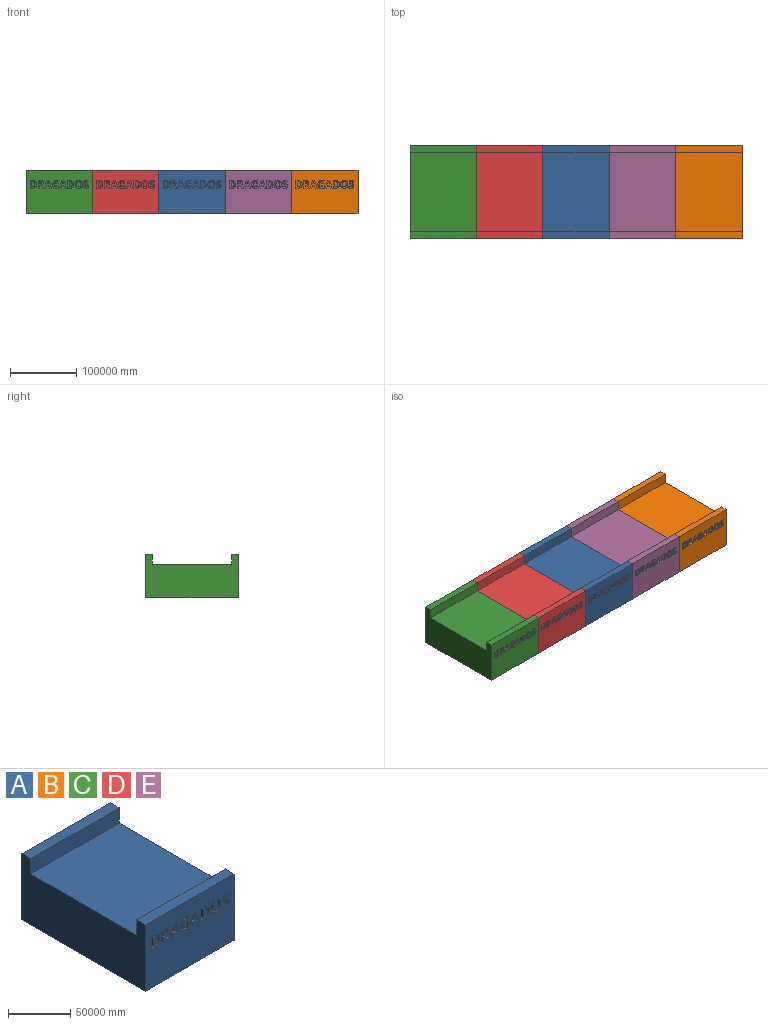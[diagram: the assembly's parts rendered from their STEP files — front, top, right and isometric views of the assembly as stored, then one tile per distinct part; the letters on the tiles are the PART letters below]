
ASSEMBLY  parts=5 mates=4
PART A: 152 faces, bbox 100000x140000x65000 mm
  f0: plane 100000x65000mm, normal (0,-1,0), area 5889989465.6mm2, adj f2,f3,f4,f9,f10,f11,f12,f13
  f1: plane 120000x100000mm, normal (0,0,1), area 12000000000mm2, adj f2,f4,f6,f8
  f2: plane 140000x65000mm, normal (-1,0,0), area 7300000000mm2, adj f0,f1,f3,f5,f6,f7,f8,f9
  f3: plane 140000x100000mm, normal (0,0,-1), area 14000000000mm2, adj f0,f2,f4,f5
  f4: plane 140000x65000mm, normal (1,0,0), area 7300000000mm2, adj f0,f1,f3,f5,f6,f7,f8,f9
  f5: plane 100000x65000mm, normal (0,1,0), area 6500000000mm2, adj f2,f3,f4,f7
  f6: plane 100000x15000mm, normal (0,-1,0), area 1500000000mm2, adj f1,f2,f4,f7
  f7: plane 100000x10000mm, normal (0,0,1), area 1000000000mm2, adj f2,f4,f5,f6
  f8: plane 100000x15000mm, normal (0,1,0), area 1500000000mm2, adj f1,f2,f4,f9
  f9: plane 100000x10000mm, normal (0,0,1), area 1000000000mm2, adj f0,f2,f4,f8
  f10: plane 4511.8x3000mm, normal (0,0,-1), area 13535406.6mm2, adj f0,f11,f28,f29
  f11: plane 3000x2008.29mm, normal (1,0,0), area 6024861.1mm2, adj f0,f10,f12,f29
  f12: plane 3000x2155.11mm, normal (0,0,1), area 6465340.4mm2, adj f0,f11,f13,f29
  f13: plane 3000x2371.62mm, normal (1,0,0), area 7114860.7mm2, adj f0,f12,f14,f29
  f14: extruded ~3000x1532.97mm, area 4629580.4mm2, adj f0,f13,f15,f29
  f15: extruded ~3000x2203.64mm, area 7506016mm2, adj f0,f14,f16,f29
  f16: extruded ~3000x2827.03mm, area 8939362.1mm2, adj f0,f15,f17,f29
  f17: extruded ~3000x2822.05mm, area 9132796.1mm2, adj f0,f16,f18,f29
  f18: extruded ~3000x2503.52mm, area 8406838mm2, adj f0,f17,f19,f29
  f19: extruded ~3000x2590.62mm, area 8066421.4mm2, adj f0,f18,f20,f29
  f20: plane 3000x1928.65mm, normal (-0.92,0,0.38), area 6265491.2mm2, adj f0,f19,f21,f29
  f21: extruded ~3377.01x3000mm, area 10418684.1mm2, adj f0,f20,f22,f29
  f22: extruded ~4364.98x3000mm, area 14252224.5mm2, adj f0,f21,f23,f29
  f23: extruded ~4291.56x3000mm, area 14101973.1mm2, adj f0,f22,f24,f29
  f24: extruded ~4345.07x3000mm, area 13969649.8mm2, adj f0,f23,f25,f29
  f25: extruded ~3930.72x3000mm, area 13034389.8mm2, adj f0,f24,f26,f29
  f26: extruded ~3000x1978.42mm, area 5956492.1mm2, adj f0,f25,f27,f29
  f27: extruded ~3000x2065.52mm, area 6384867.5mm2, adj f0,f26,f28,f29
  f28: plane 5895.45x3000mm, normal (-1,0,0), area 17686364.2mm2, adj f0,f10,f27,f29
  f29: plane 11688.88x9332.19mm, normal (0,-1,0), area 62986172mm2, adj f10,f11,f12,f13,f14,f15,f16,f17
  f30: extruded ~3000x2870.58mm, area 9030077.2mm2, adj f31,f43,f44,f147
  f31: extruded ~3000x2871.83mm, area 9041235.7mm2, adj f30,f32,f44,f147
  f32: extruded ~3000x2168.8mm, area 7406378.6mm2, adj f31,f33,f44,f147
  f33: extruded ~3839.88x3000mm, area 16403148.1mm2, adj f32,f34,f44,f147
  f34: extruded ~3834.91x3000mm, area 16424551mm2, adj f33,f43,f44,f147
  f35: extruded ~4341.33x3000mm, area 14012505mm2, adj f0,f36,f42,f44
  f36: extruded ~4338.85x3000mm, area 13992602.8mm2, adj f0,f35,f37,f44
  f37: extruded ~4009.11x3000mm, area 13243213.6mm2, adj f0,f36,f38,f44
  f38: extruded ~4024.04x3000mm, area 13263273.8mm2, adj f0,f37,f39,f44
  f39: extruded ~4336.36x3000mm, area 14008077.7mm2, adj f0,f38,f40,f44
  f40: extruded ~4356.27x3000mm, area 14055744mm2, adj f0,f39,f41,f44
  f41: extruded ~4012.84x3000mm, area 13261248.6mm2, adj f0,f40,f42,f44
  f42: extruded ~4012.84x3000mm, area 13261248.6mm2, adj f0,f35,f41,f44
  f43: extruded ~3000x2161.34mm, area 7382216.9mm2, adj f30,f34,f44,f147
  f44: plane 11706.3x10825.34mm, normal (0,-1,0), area 67703911.6mm2, adj f30,f31,f32,f33,f34,f35,f36,f37
  f45: extruded ~3663.2x3235.16mm, area 16809076.1mm2, adj f46,f56,f57,f148
  f46: extruded ~3740.34x3484.02mm, area 17594489.8mm2, adj f45,f47,f57,f148
  f47: plane 3000x1032.76mm, normal (0,0,-1), area 3098286.7mm2, adj f46,f48,f57,f148
  f48: plane 7403.54x3000mm, normal (-1,0,0), area 22210609.3mm2, adj f47,f56,f57,f148
  f49: extruded ~4300.27x3000mm, area 14174793.3mm2, adj f0,f50,f55,f57
  f50: extruded ~4107.41x3000mm, area 13544800.3mm2, adj f0,f49,f51,f57
  f51: extruded ~4325.16x3000mm, area 14051984.7mm2, adj f0,f50,f52,f57
  f52: plane 3568.63x3000mm, normal (0,0,-1), area 10705887mm2, adj f0,f51,f53,f57
  f53: plane 11370.34x3000mm, normal (1,0,0), area 34111016.4mm2, adj f0,f52,f54,f57
  f54: plane 3220.23x3000mm, normal (0,0,1), area 9660681.8mm2, adj f0,f53,f55,f57
  f55: extruded ~4615.08x3000mm, area 14906133.2mm2, adj f0,f49,f54,f57
  f56: plane 3000x1281.62mm, normal (0,0,1), area 3844861.8mm2, adj f45,f48,f57,f148
  f57: plane 11370.34x9434.22mm, normal (0,-1,0), area 65817079.6mm2, adj f45,f46,f47,f48,f49,f50,f51,f52
  f58: extruded ~4160.91x3000mm, area 13065876.7mm2, adj f59,f69,f70,f149
  f59: plane 3000x2961.41mm, normal (0,0,-1), area 8884243.7mm2, adj f58,f60,f70,f149
  f60: extruded ~4922.42x3000mm, area 15410954.9mm2, adj f59,f69,f70,f149
  f61: plane 3000x2707.58mm, normal (0.96,0,0.29), area 8490318.5mm2, adj f0,f62,f68,f70
  f62: plane 3000x2598.08mm, normal (0,0,1), area 7794244.1mm2, adj f0,f61,f63,f70
  f63: plane 11417.62x4029.02mm, normal (-0.94,0,-0.33), area 36322935mm2, adj f0,f62,f64,f70
  f64: plane 3000x2946.48mm, normal (0,0,-1), area 8839449.2mm2, adj f0,f63,f65,f70
  f65: plane 11417.62x4014.09mm, normal (0.94,0,-0.33), area 36308053.4mm2, adj f0,f64,f66,f70
  f66: plane 3000x2598.08mm, normal (0,0,1), area 7794244.1mm2, adj f0,f65,f67,f70
  f67: plane 3000x2707.58mm, normal (-0.96,0,0.29), area 8490318.5mm2, adj f0,f66,f68,f70
  f68: plane 4145.98x3000mm, normal (0,0,1), area 12437941.2mm2, adj f0,f61,f67,f70
  f69: extruded ~3000x761.51mm, area 2367510.5mm2, adj f58,f60,f70,f149
  f70: plane 11417.62x10989.59mm, normal (0,-1,0), area 58950877mm2, adj f58,f59,f60,f61,f62,f63,f64,f65
  f71: extruded ~3000x2427.61mm, area 8303820.4mm2, adj f0,f72,f98,f99
  f72: extruded ~3000x1877.64mm, area 6017220.3mm2, adj f0,f71,f73,f99
  f73: extruded ~3000x2186.22mm, area 8069418.4mm2, adj f0,f72,f74,f99
  f74: extruded ~3000x1526.75mm, area 5169060.9mm2, adj f0,f73,f75,f99
  f75: extruded ~3000x470.34mm, area 1985542.8mm2, adj f0,f74,f76,f99
  f76: extruded ~3000x556.2mm, area 1749833.2mm2, adj f0,f75,f77,f99
  f77: extruded ~3000x831.19mm, area 2815640.2mm2, adj f0,f76,f78,f99
  f78: extruded ~3000x1050.18mm, area 3364291mm2, adj f0,f77,f79,f99
  f79: extruded ~3000x1169.63mm, area 3545737.4mm2, adj f0,f78,f80,f99
  f80: extruded ~3000x1505.59mm, area 4783799.7mm2, adj f0,f79,f81,f99
  f81: plane 3000x1876.39mm, normal (-0.92,0,0.38), area 6092071.1mm2, adj f0,f80,f82,f99
  f82: extruded ~3000x1683.53mm, area 5356881.6mm2, adj f0,f81,f83,f99
  f83: extruded ~3000x1690.99mm, area 5125435.5mm2, adj f0,f82,f84,f99
  f84: extruded ~3000x2827.03mm, area 9053745.9mm2, adj f0,f83,f85,f99
  f85: extruded ~3000x2372.86mm, area 8020942mm2, adj f0,f84,f86,f99
  f86: extruded ~3000x1398.58mm, area 4340097.6mm2, adj f0,f85,f87,f99
  f87: extruded ~3000x1050.18mm, area 4044865.9mm2, adj f0,f86,f88,f99
  f88: extruded ~3000x1561.59mm, area 5484625.9mm2, adj f0,f87,f89,f99
  f89: extruded ~3000x1474.49mm, area 4993462.5mm2, adj f0,f88,f90,f99
  f90: extruded ~3000x548.73mm, area 2242214.9mm2, adj f0,f89,f91,f99
  f91: extruded ~3000x594.77mm, area 1901623.8mm2, adj f0,f90,f92,f99
  f92: extruded ~3000x902.11mm, area 3117233.3mm2, adj f0,f91,f93,f99
  f93: extruded ~3000x1215.67mm, area 3817270.7mm2, adj f0,f92,f94,f99
  f94: extruded ~3000x1459.55mm, area 4435350.4mm2, adj f0,f93,f95,f99
  f95: extruded ~3000x1947.32mm, area 6239494.7mm2, adj f0,f94,f96,f99
  f96: plane 3000x2239.73mm, normal (1,0,0), area 6719175.9mm2, adj f0,f95,f97,f99
  f97: extruded ~3220.23x3000mm, area 9965344.2mm2, adj f0,f96,f98,f99
  f98: extruded ~3082.11x3000mm, area 9807859.6mm2, adj f0,f71,f97,f99
  f99: plane 11688.88x7411mm, normal (0,-1,0), area 48752152.3mm2, adj f71,f72,f73,f74,f75,f76,f77,f78
  f100: extruded ~3663.2x3235.16mm, area 16809076.1mm2, adj f101,f111,f112,f150
  f101: extruded ~3740.34x3484.02mm, area 17594489.8mm2, adj f100,f102,f112,f150
  f102: plane 3000x1032.76mm, normal (0,0,-1), area 3098286.7mm2, adj f101,f103,f112,f150
  f103: plane 7403.54x3000mm, normal (-1,0,0), area 22210609.3mm2, adj f102,f111,f112,f150
  f104: extruded ~4300.27x3000mm, area 14174793.3mm2, adj f0,f105,f110,f112
  f105: extruded ~4107.41x3000mm, area 13544800.3mm2, adj f0,f104,f106,f112
  f106: extruded ~4325.16x3000mm, area 14051984.7mm2, adj f0,f105,f107,f112
  f107: plane 3568.63x3000mm, normal (0,0,-1), area 10705887mm2, adj f0,f106,f108,f112
  f108: plane 11370.34x3000mm, normal (1,0,0), area 34111016.4mm2, adj f0,f107,f109,f112
  f109: plane 3220.23x3000mm, normal (0,0,1), area 9660681.8mm2, adj f0,f108,f110,f112
  f110: extruded ~4615.08x3000mm, area 14906133.2mm2, adj f0,f104,f109,f112
  f111: plane 3000x1281.62mm, normal (0,0,1), area 3844861.8mm2, adj f100,f103,f112,f150
  f112: plane 11370.34x9434.22mm, normal (0,-1,0), area 65817079.6mm2, adj f100,f101,f102,f103,f104,f105,f106,f107
  f113: plane 4362.49x3000mm, normal (-1,0,0), area 13087461.5mm2, adj f0,f114,f131,f132
  f114: plane 3000x1281.62mm, normal (0,0,1), area 3844861.8mm2, adj f0,f113,f115,f132
  f115: plane 4362.49x3000mm, normal (0.85,0,0.53), area 15415085.6mm2, adj f0,f114,f116,f132
  f116: plane 3000x2675.23mm, normal (0,0,1), area 8025682.3mm2, adj f0,f115,f117,f132
  f117: extruded ~4954.77x3344.66mm, area 17934115.7mm2, adj f0,f116,f118,f132
  f118: extruded ~3000x1564.08mm, area 6034781mm2, adj f0,f117,f119,f132
  f119: extruded ~3000x1784.31mm, area 5695065.4mm2, adj f0,f118,f120,f132
  f120: extruded ~3000x2563.24mm, area 8707609.6mm2, adj f0,f119,f121,f132
  f121: extruded ~3430.51x3000mm, area 10776834.6mm2, adj f0,f120,f122,f132
  f122: plane 3312.31x3000mm, normal (0,0,-1), area 9936914.6mm2, adj f0,f121,f123,f132
  f123: plane 11370.34x3000mm, normal (1,0,0), area 34111016.4mm2, adj f0,f122,f131,f132
  f124: plane 3000x776.44mm, normal (0,0,-1), area 2329314.3mm2, adj f125,f130,f132,f133
  f125: plane 3070.91x3000mm, normal (-1,0,0), area 9212736.7mm2, adj f124,f126,f132,f133
  f126: plane 3000x731.64mm, normal (0,0,1), area 2194930.8mm2, adj f125,f127,f132,f133
  f127: extruded ~3000x1720.86mm, area 5325056.4mm2, adj f126,f128,f132,f133
  f128: extruded ~3000x1150.97mm, area 4022426.4mm2, adj f127,f129,f132,f133
  f129: extruded ~3000x1197.01mm, area 4112647.7mm2, adj f128,f130,f132,f133
  f130: extruded ~3000x1688.5mm, area 5268649.4mm2, adj f124,f129,f132,f133
  f131: plane 3000x2411.44mm, normal (0,0,1), area 7234312.7mm2, adj f0,f113,f123,f132
  f132: plane 11370.34x9083.33mm, normal (0,-1,0), area 63126842mm2, adj f113,f114,f115,f116,f117,f118,f119,f120
  f133: plane 3070.91x3008.7mm, normal (0,-1,0), area 8156719.4mm2, adj f124,f125,f126,f127,f128,f129,f130
  f134: extruded ~4160.91x3000mm, area 13065876.7mm2, adj f135,f145,f146,f151
  f135: plane 3000x2961.41mm, normal (0,0,-1), area 8884243.7mm2, adj f134,f136,f146,f151
  f136: extruded ~4922.42x3000mm, area 15410954.9mm2, adj f135,f145,f146,f151
  f137: plane 3000x2707.58mm, normal (0.96,0,0.29), area 8490318.5mm2, adj f0,f138,f144,f146
  f138: plane 3000x2598.08mm, normal (0,0,1), area 7794244.1mm2, adj f0,f137,f139,f146
  f139: plane 11417.62x4029.02mm, normal (-0.94,0,-0.33), area 36322935mm2, adj f0,f138,f140,f146
  f140: plane 3000x2946.48mm, normal (0,0,-1), area 8839449.2mm2, adj f0,f139,f141,f146
  f141: plane 11417.62x4014.09mm, normal (0.94,0,-0.33), area 36308053.4mm2, adj f0,f140,f142,f146
  f142: plane 3000x2598.08mm, normal (0,0,1), area 7794244.1mm2, adj f0,f141,f143,f146
  f143: plane 3000x2707.58mm, normal (-0.96,0,0.29), area 8490318.5mm2, adj f0,f142,f144,f146
  f144: plane 4145.98x3000mm, normal (0,0,1), area 12437941.2mm2, adj f0,f137,f143,f146
  f145: extruded ~3000x761.51mm, area 2367510.5mm2, adj f134,f136,f146,f151
  f146: plane 11417.62x10989.59mm, normal (0,-1,0), area 58950877mm2, adj f134,f135,f136,f137,f138,f139,f140,f141
  f147: plane 7674.79x5768.54mm, normal (0,-1,0), area 36859398.6mm2, adj f30,f31,f32,f33,f34,f43
  f148: plane 7403.54x4516.78mm, normal (0,-1,0), area 29293068.7mm2, adj f45,f46,f47,f48,f56
  f149: plane 4922.42x2961.41mm, normal (0,-1,0), area 7151643.9mm2, adj f58,f59,f60,f69
  f150: plane 7403.54x4516.78mm, normal (0,-1,0), area 29293068.7mm2, adj f100,f101,f102,f103,f111
  f151: plane 4922.42x2961.41mm, normal (0,-1,0), area 7151643.9mm2, adj f134,f135,f136,f145
PART B: same geometry as A
PART C: same geometry as A
PART D: same geometry as A
PART E: same geometry as A
PLACE A t=(200000,0,0)mm
PLACE B t=(400000,0,0)mm
PLACE C at identity fixed
PLACE D t=(100000,0,0)mm
PLACE E t=(300000,0,0)mm
MATE fastened C.f4 <-> D.f2  axis (1,0,0) through (95000.32,0,24240)mm
MATE fastened D.f4 <-> A.f2  axis (1,0,0) through (195000.32,0,24240)mm
MATE fastened E.f2 <-> A.f4  axis (-1,0,0) through (295000.32,0,24240)mm
MATE fastened B.f2 <-> E.f4  axis (-1,0,0) through (395000.32,0,24240)mm
